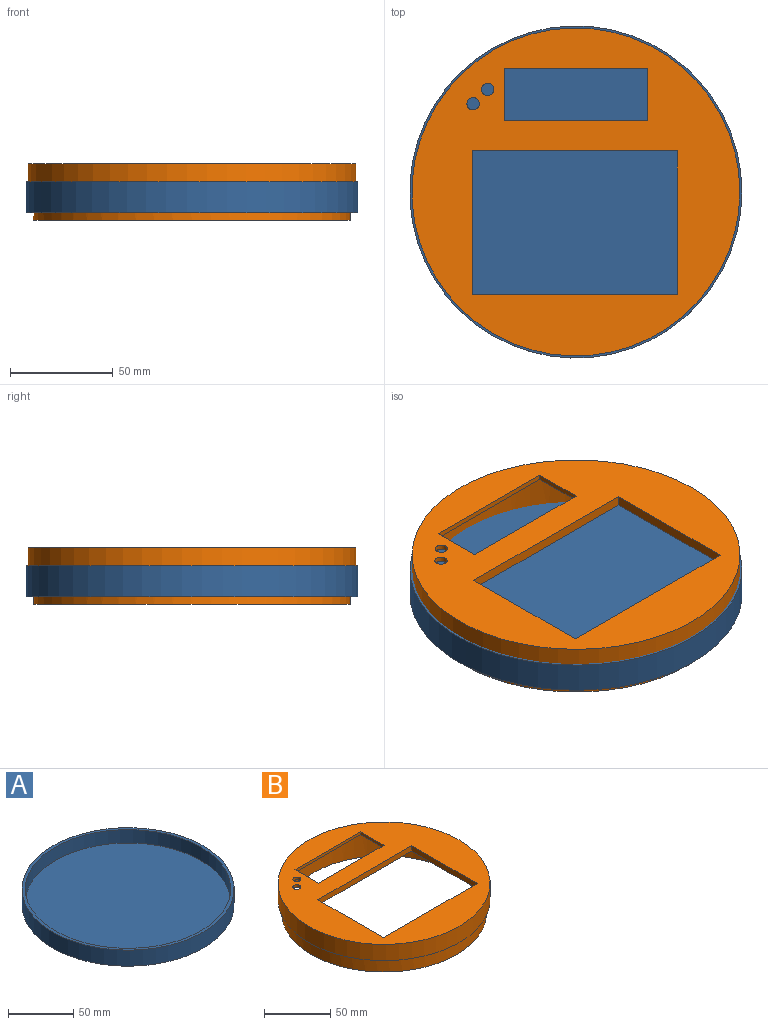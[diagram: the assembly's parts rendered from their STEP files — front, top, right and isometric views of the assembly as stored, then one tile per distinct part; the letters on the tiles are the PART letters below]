
ASSEMBLY  parts=2 mates=1
PART A: 5 faces, bbox 162x162x15 mm
  f0: cylinder r=81mm len=162mm, axis (0,0,-1), area 7634.1mm2, adj f1,f2
  f1: plane 162x162mm, normal (0,0,1), area 1252.7mm2, adj f0,f3
  f2: plane 162x162mm, normal (0,0,-1), area 20612mm2, adj f0
  f3: cylinder r=78.5mm len=157mm, axis (0,0,-1), area 6165.4mm2, adj f1,f4
  f4: plane 157x157mm, normal (0,0,1), area 19359.3mm2, adj f3
PART B: 24 faces, bbox 160x160x27.5 mm
  f0: plane 25x2.5mm, normal (1,0,0), area 62.5mm2, adj f1,f3,f10,f21
  f1: plane 70x2.5mm, normal (0,-1,0), area 175mm2, adj f0,f2,f10,f21
  f2: plane 25x2.5mm, normal (-1,0,0), area 62.5mm2, adj f1,f3,f10,f21
  f3: plane 70x2.5mm, normal (0,1,0), area 175mm2, adj f0,f2,f10,f21
  f4: plane 105x75mm, normal (0,0,-1), area 875mm2, adj f5,f6,f7,f8,f17,f18,f19,f20
  f5: plane 70x5mm, normal (1,0,0), area 350mm2, adj f4,f6,f8,f10
  f6: plane 100x5mm, normal (0,-1,0), area 500mm2, adj f4,f5,f7,f10
  f7: plane 70x5mm, normal (-1,0,0), area 350mm2, adj f4,f6,f8,f10
  f8: plane 100x5mm, normal (0,1,0), area 500mm2, adj f4,f5,f7,f10
  f9: cylinder r=80mm len=160mm, axis (0,0,-1), area 7539.8mm2, adj f10,f11
  f10: plane 160x160mm, normal (0,0,1), area 11299.6mm2, adj f0,f1,f2,f3,f5,f6,f7,f8
  f11: plane 160x160mm, normal (0,0,-1), area 1237mm2, adj f9,f12
  f12: cylinder r=77.5mm len=155mm, axis (0,0,-1), area 6086.8mm2, adj f11,f13
  f13: plane 155x155mm, normal (0,0,-1), area 121.5mm2, adj f12,f15
  f14: plane 154.5x154.5mm, normal (0,0,-1), area 1193.8mm2, adj f15,f16
  f15: cylinder r=77.25mm len=154.5mm, axis (0,0,1), area 12134.4mm2, adj f13,f14
  f16: cylinder r=74.75mm len=149.5mm, axis (0,0,1), area 11741.7mm2, adj f14,f21
  f17: plane 75x2.5mm, normal (-1,0,0), area 187.5mm2, adj f4,f18,f20,f21
  f18: plane 105x2.5mm, normal (0,1,0), area 262.5mm2, adj f4,f17,f19,f21
  f19: plane 75x2.5mm, normal (1,0,0), area 187.5mm2, adj f4,f18,f20,f21
  f20: plane 105x2.5mm, normal (0,-1,0), area 262.5mm2, adj f4,f17,f19,f21
  f21: plane 149.5x149.5mm, normal (0,0,-1), area 7872.3mm2, adj f0,f1,f2,f3,f16,f17,f18,f19
  f22: cylinder r=3mm len=6mm, axis (0,0,1), area 47.1mm2, adj f10,f21
  f23: cylinder r=3mm len=6mm, axis (0,0,1), area 47.1mm2, adj f10,f21
PLACE A at identity
PLACE B t=(0,0,8.75)mm
MATE fastened B.f15 <-> A.f0  axis (0,0,1) through (0,0,8.75)mm
